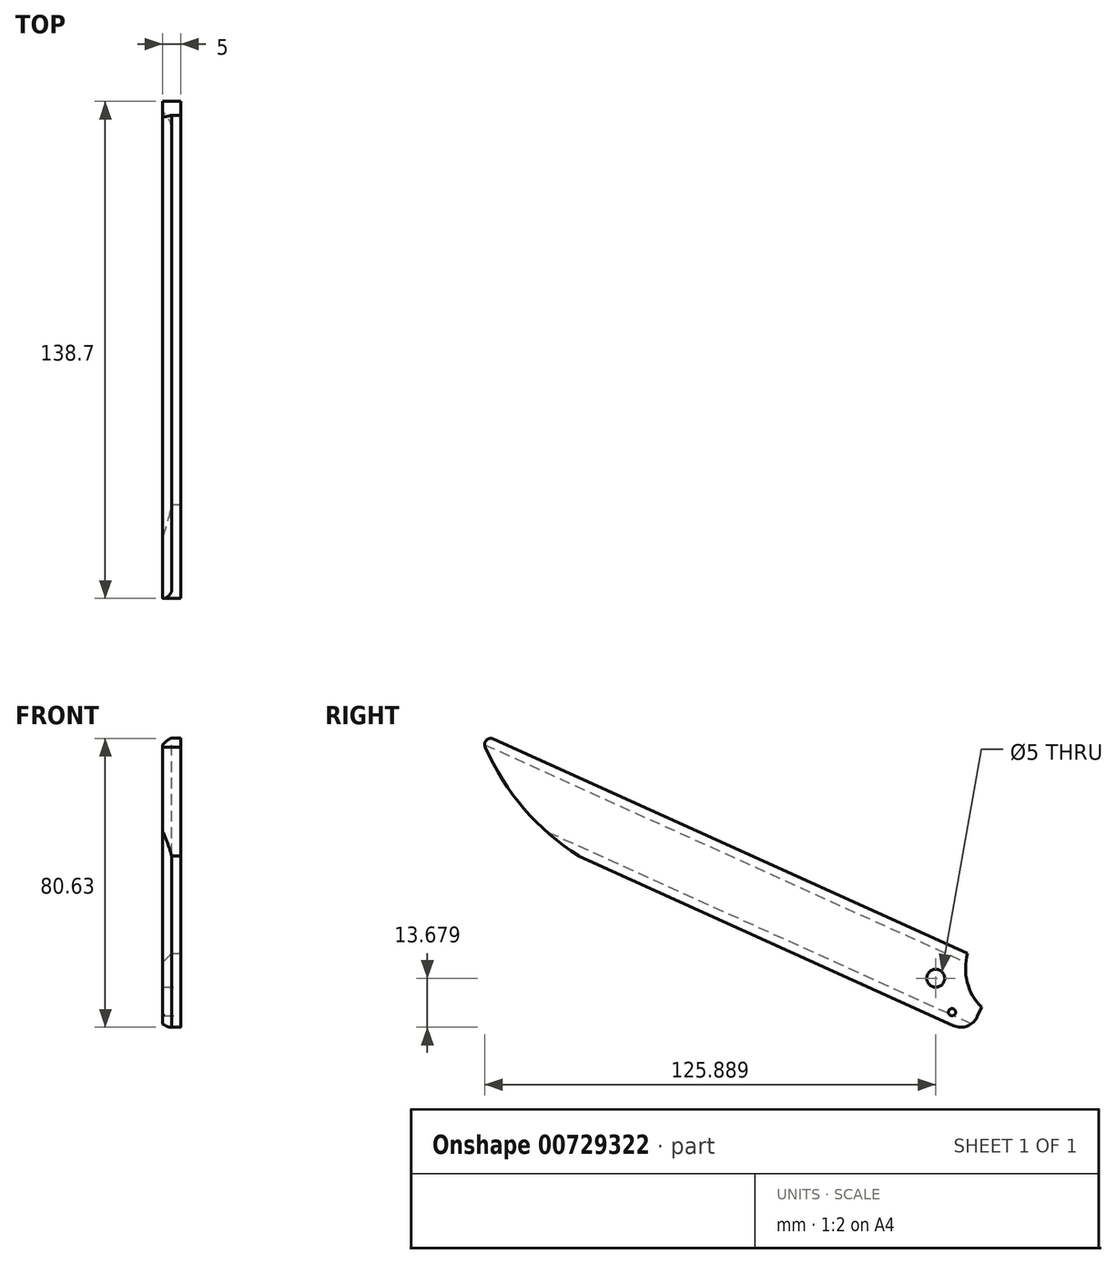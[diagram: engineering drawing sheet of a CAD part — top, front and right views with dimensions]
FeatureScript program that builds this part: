
annotation { "Feature Type Name" : "Feature", "Feature Type Description" : "" }
export const myFeature = defineFeature(function(context is Context, id is Id, definition is map)
    precondition{}
    {
        {
            var Q0;
            Q0=qCreatedBy(makeId("Right.planeOp"),FACE);
            var sketch = newSketch(context, id + "F0", { "sketchPlane" : qUnion([Q0])});
            skLineSegment(sketch, "E0", {"start": v(-133.72, 3.82) * mm, "end": v(-238.35, 51.14) * mm});
            skLineSegment(sketch, "E1", {"start": v(-262.15, 83.85) * mm, "end": v(-129.77, 23.98) * mm});
            skLineSegment(sketch, "E2", {"start": v(-125.9, 8.98) * mm, "end": v(-127.1, 6.31) * mm});
            skCircle(sketch, "E3", {"center": v(-138.71, 17.05) * mm, "radius": 2.5 * mm});
            skCircle(sketch, "E4.0", {"center": v(-138.71, 17.05) * mm, "radius": 10.5 * mm, "construction": true});
            skLineSegment(sketch, "E5.0", {"start": v(-141.05, 12.77) * mm, "end": v(-129.77, 7.66) * mm, "construction": true});
            skCircle(sketch, "E6", {"center": v(-132.24, 8.78) * mm, "radius": 1 * mm, "construction": true});
            skPoint(sketch, "E7.visualSharp", {"position": v(-129.16, 1.76) * mm});
            skArc(sketch, "E7.filletArc", {"start": v(-133.72, 3.82) * mm, "mid": v(-129.9, 3.7) * mm, "end": v(-127.1, 6.31) * mm});
            skPoint(sketch, "E8.visualSharp", {"position": v(-120.92, 19.98) * mm});
            skArc(sketch, "E9", {"start": v(-264.5, 81.67) * mm, "mid": v(-253.7, 64.46) * mm, "end": v(-238.35, 51.14) * mm});
            skPoint(sketch, "E10.start.orphan", {"position": v(-256.73, 59.45) * mm});
            skLineSegment(sketch, "E11", {"start": v(-262.15, 83.85) * mm, "end": v(-224.51, 66.83) * mm});
            skArc(sketch, "E12", {"start": v(-262.15, 83.85) * mm, "mid": v(-264.13, 83.46) * mm, "end": v(-264.4, 81.47) * mm});
            skLineSegment(sketch, "E13", {"start": v(-138.71, 17.05) * mm, "end": v(-142.83, 7.94) * mm, "construction": true});
            skCircle(sketch, "E14", {"center": v(-138.71, 17.05) * mm, "radius": 117.85 * mm, "construction": true});
            skLineSegment(sketch, "E15", {"start": v(-273.63, 72.67) * mm, "end": v(-218.97, 47.95) * mm, "construction": true});
            skCircle(sketch, "E16", {"center": v(-248.03, 61.09) * mm, "radius": 1 * mm, "construction": true});
            skArc(sketch, "E17", {"start": v(-129.77, 23.98) * mm, "mid": v(-129.92, 15.94) * mm, "end": v(-125.9, 8.98) * mm});
            skLineSegment(sketch, "E18", {"start": v(-138.71, 17.05) * mm, "end": v(-131.38, 13.73) * mm, "construction": true});
            skLineSegment(sketch, "E19", {"start": v(-131.38, 13.73) * mm, "end": v(-134.16, 7.59) * mm, "construction": true});
            skCircle(sketch, "E20", {"center": v(-134.16, 7.59) * mm, "radius": 1 * mm});
            skSolve(sketch);
        }
        {
            var Q0;
            Q0=qSketchRegion(id+"F0",true);
            extrude(context, id + "F1", {"entities" : qUnion([Q0]), "oppositeDirection" : true, "depth" : 5 * mm, "offsetDistance" : 25 * mm});
        }
        {
            var Q0;
            Q0=makeQuery(id+"F1.opExtrude","CAP_EDGE",EDGE,{"disambiguationData":[OSD([sQuery(id+"F0.wireOp",EDGE,"E0")])],"isStart":false});
            var Q1;
            Q1=makeQuery(id+"F1.opExtrude","CAP_EDGE",EDGE,{"disambiguationData":[OSD([sQuery(id+"F0.wireOp",EDGE,"E1"),sQuery(id+"F0.wireOp",EDGE,"E11")])],"isStart":false});
            chamfer(context, id + "F2", {"entities" : qUnion([Q0, Q1]), "width" : 2.5 * mm});
        }
    });
